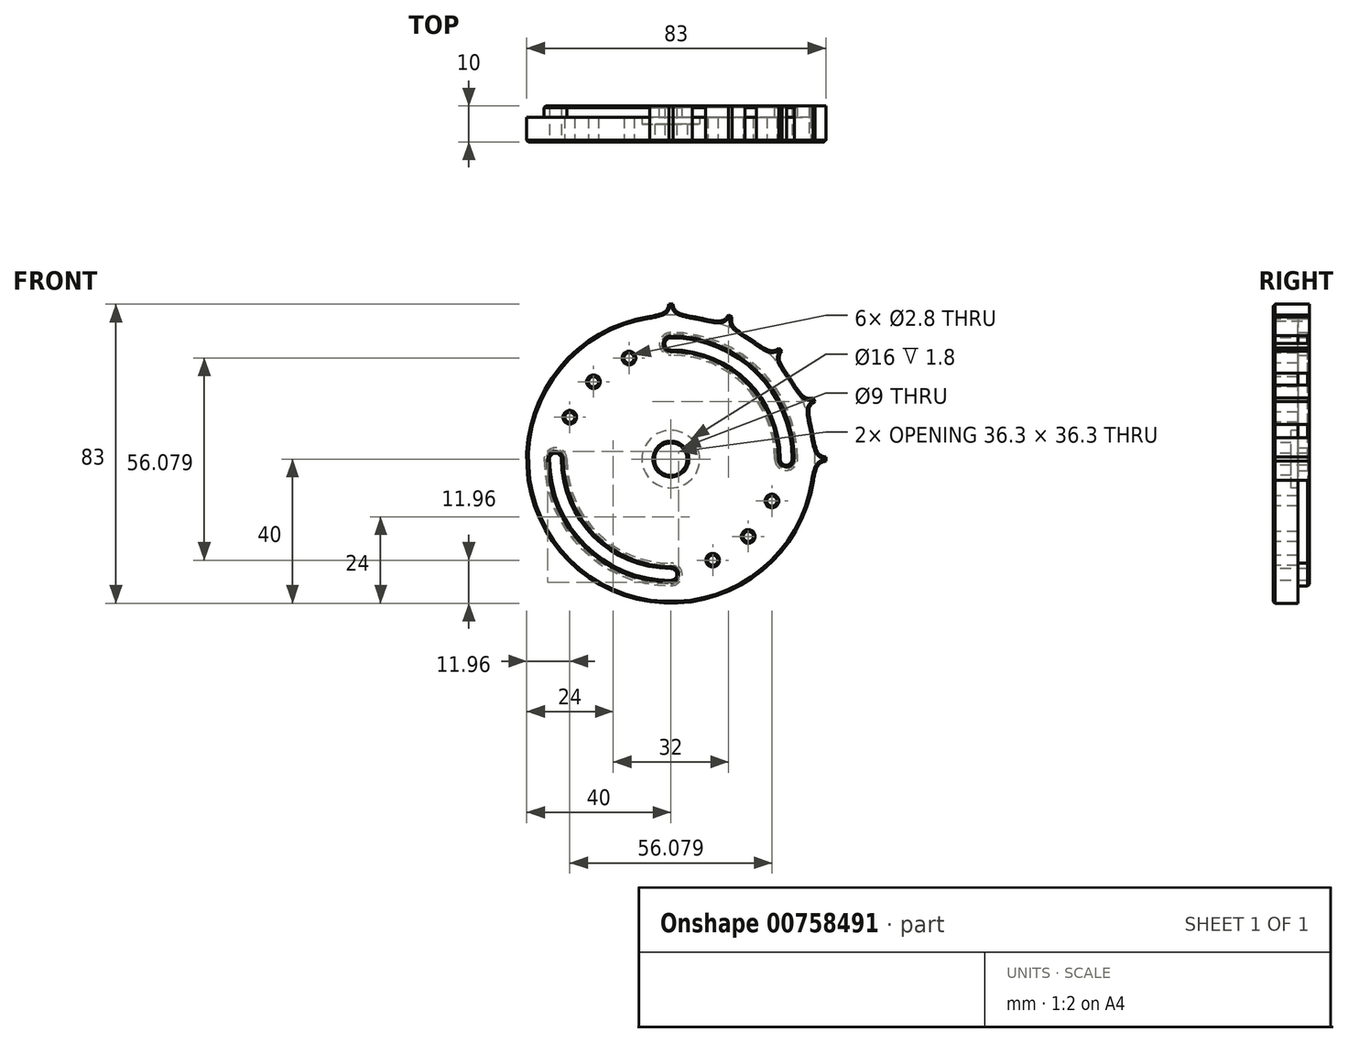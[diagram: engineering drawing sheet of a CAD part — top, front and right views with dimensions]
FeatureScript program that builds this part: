
annotation { "Feature Type Name" : "Feature", "Feature Type Description" : "" }
export const myFeature = defineFeature(function(context is Context, id is Id, definition is map)
    precondition{}
    {
        {
            var Q0;
            Q0=qCreatedBy(makeId("Front.planeOp"),FACE);
            var sketch = newSketch(context, id + "F0", { "sketchPlane" : qUnion([Q0])});
            skCircle(sketch, "E0", {"center": v(0, 0) * mm, "radius": 4.5 * mm});
            skCircle(sketch, "E1", {"center": v(0, 0) * mm, "radius": 40 * mm});
            skCircle(sketch, "E2", {"center": v(-32, 0) * mm, "radius": 1.65 * mm});
            skCircle(sketch, "E3.1.0", {"center": v(0, -32) * mm, "radius": 1.65 * mm});
            skCircle(sketch, "E3.2.0", {"center": v(32, 0) * mm, "radius": 1.65 * mm});
            skCircle(sketch, "E3.3.0", {"center": v(0, 32) * mm, "radius": 1.65 * mm});
            skCircle(sketch, "E4", {"center": v(0, 0) * mm, "radius": 8 * mm});
            skCircle(sketch, "E5", {"center": v(0, 0) * mm, "radius": 25 * mm});
            skCircle(sketch, "E6", {"center": v(0, 0) * mm, "radius": 33.65 * mm});
            skCircle(sketch, "E7", {"center": v(0, 0) * mm, "radius": 30.35 * mm});
            skCircle(sketch, "E8", {"center": v(-11.61, 28.04) * mm, "radius": 1.4 * mm});
            skCircle(sketch, "E9", {"center": v(-21.46, 21.46) * mm, "radius": 1.4 * mm});
            skLineSegment(sketch, "E10", {"start": v(0, 0) * mm, "end": v(-21.46, 21.46) * mm, "construction": true});
            skLineSegment(sketch, "E11", {"start": v(0, 0) * mm, "end": v(-11.61, 28.04) * mm, "construction": true});
            skCircle(sketch, "E12.MirrorC", {"center": v(-28.04, 11.61) * mm, "radius": 1.4 * mm});
            skCircle(sketch, "E13.1.0", {"center": v(11.61, -28.04) * mm, "radius": 1.4 * mm});
            skCircle(sketch, "E13.1.1", {"center": v(21.46, -21.46) * mm, "radius": 1.4 * mm});
            skCircle(sketch, "E13.1.2", {"center": v(28.04, -11.61) * mm, "radius": 1.4 * mm});
            skFitSpline(sketch, "E14", {"points": [v(43, 0.56) * mm, v(39.56, 5.91) * mm], "startDerivative": vector(-7.22, 1.17) * mm, "endDerivative": vector(-2.2, 10.93) * mm});
            skLineSegment(sketch, "E15", {"start": v(43, 0.56) * mm, "end": v(43, 0) * mm});
            skLineSegment(sketch, "E16.MirrorCS", {"start": v(43, -0.56) * mm, "end": v(43, 0) * mm});
            skFitSpline(sketch, "E17.MirrorCS", {"points": [v(43, -0.56) * mm, v(39.56, -5.91) * mm], "startDerivative": vector(-7.22, -1.17) * mm, "endDerivative": vector(-2.2, -10.93) * mm});
            skSolve(sketch);
        }
        {
            var Q0;
            Q0=makeQuery(id+"F0.imprint","IMPRINT",FACE,{"disambiguationData":[TD([[makeQuery(id+"F0.imprint","IMPRINT",EDGE,{"derivedFrom":sQuery(id+"F0.wireOp",EDGE,"E1")}),1.0]])]});
            var Q1;
            {var subQ0=sQuery(id+"F0.wireOp",EDGE,"E6");var subQ1=sQuery(id+"F0.wireOp",EDGE,"E2");var subQ2=makeQuery(id+"F0.imprint","INTERSECT",VERTEX,{"derivedFrom":[subQ1,subQ0]});Q1=makeQuery(id+"F0.imprint","IMPRINT",FACE,{"disambiguationData":[TD([[makeQuery(id+"F0.imprint","IMPRINT",EDGE,{"disambiguationData":[TD([[subQ2,1.0]])],"derivedFrom":subQ1}),-1.0]])]});}
            var Q2;
            Q2=makeQuery(id+"F0.imprint","IMPRINT",FACE,{"disambiguationData":[TD([[makeQuery(id+"F0.imprint","IMPRINT",EDGE,{"derivedFrom":sQuery(id+"F0.wireOp",EDGE,"E5")}),-1.0]])]});
            var Q3;
            {var subQ0=sQuery(id+"F0.wireOp",EDGE,"E6");var subQ1=sQuery(id+"F0.wireOp",EDGE,"E3.1.0");var subQ2=makeQuery(id+"F0.imprint","INTERSECT",VERTEX,{"derivedFrom":[subQ1,subQ0]});Q3=makeQuery(id+"F0.imprint","IMPRINT",FACE,{"disambiguationData":[TD([[makeQuery(id+"F0.imprint","IMPRINT",EDGE,{"disambiguationData":[TD([[subQ2,-1.0]])],"derivedFrom":subQ1}),-1.0]])]});}
            var Q4;
            Q4=makeQuery(id+"F0.imprint","IMPRINT",FACE,{"disambiguationData":[TD([[makeQuery(id+"F0.imprint","IMPRINT",EDGE,{"derivedFrom":sQuery(id+"F0.wireOp",EDGE,"E4")}),-1.0]])]});
            extrude(context, id + "F1", {"entities" : qUnion([Q0, Q1, Q2, Q3, Q4]), "oppositeDirection" : true, "depth" : 10 * mm, "offsetDistance" : 25 * mm});
        }
        {
            var Q0;
            Q0=makeQuery(id+"F0.imprint","IMPRINT",FACE,{"disambiguationData":[TD([[makeQuery(id+"F0.imprint","IMPRINT",EDGE,{"derivedFrom":sQuery(id+"F0.wireOp",EDGE,"E0")}),-1.0]])]});
            extrude(context, id + "F2", {"entities" : qUnion([Q0]), "operationType" : NewBodyOperationType.ADD, "oppositeDirection" : true, "depth" : 5 * mm, "offsetDistance" : 25 * mm});
        }
        {
            var Q0;
            Q0=makeQuery(id+"F1.opExtrude","CAP_FACE",FACE,{"disambiguationData":[OSD([sQuery(id+"F0.wireOp",EDGE,"E1"),sQuery(id+"F0.wireOp",EDGE,"E2"),sQuery(id+"F0.wireOp",EDGE,"E3.1.0"),sQuery(id+"F0.wireOp",EDGE,"E3.2.0"),sQuery(id+"F0.wireOp",EDGE,"E3.3.0"),sQuery(id+"F0.wireOp",EDGE,"E4"),sQuery(id+"F0.wireOp",EDGE,"E6"),sQuery(id+"F0.wireOp",EDGE,"E7")])],"isStart":false});
            var sketch = newSketch(context, id + "F3", { "sketchPlane" : qUnion([Q0])});
            skArc(sketch, "E18.0", {"start": v(-28.85, 0) * mm, "mid": v(-20.4, 20.4) * mm, "end": v(0, 28.85) * mm});
            skArc(sketch, "E18.1", {"start": v(-28.85, 0) * mm, "mid": v(-32, -3.15) * mm, "end": v(-35.15, 0) * mm});
            skArc(sketch, "E18.2", {"start": v(-35.15, 0) * mm, "mid": v(-24.85, 24.85) * mm, "end": v(0, 35.15) * mm});
            skArc(sketch, "E18.3", {"start": v(0, 35.15) * mm, "mid": v(3.15, 32) * mm, "end": v(0, 28.85) * mm});
            skArc(sketch, "E19.0", {"start": v(28.85, 0) * mm, "mid": v(20.4, -20.4) * mm, "end": v(0, -28.85) * mm});
            skArc(sketch, "E19.1", {"start": v(28.85, 0) * mm, "mid": v(32, 3.15) * mm, "end": v(35.15, 0) * mm});
            skArc(sketch, "E19.2", {"start": v(35.15, 0) * mm, "mid": v(24.85, -24.85) * mm, "end": v(0, -35.15) * mm});
            skArc(sketch, "E19.3", {"start": v(0, -35.15) * mm, "mid": v(-3.15, -32) * mm, "end": v(0, -28.85) * mm});
            skSolve(sketch);
        }
        {
            var Q0;
            Q0=makeQuery(id+"F3.imprint","IMPRINT",FACE,{"disambiguationData":[TD([[makeQuery(id+"F3.imprint","IMPRINT",EDGE,{"derivedFrom":sQuery(id+"F3.wireOp",EDGE,"E18.0")}),1.0]])]});
            var Q1;
            Q1=makeQuery(id+"F3.imprint","IMPRINT",FACE,{"disambiguationData":[TD([[makeQuery(id+"F3.imprint","IMPRINT",EDGE,{"derivedFrom":sQuery(id+"F3.wireOp",EDGE,"E19.0")}),1.0]])]});
            extrude(context, id + "F4", {"entities" : qUnion([Q0, Q1]), "operationType" : NewBodyOperationType.REMOVE, "oppositeDirection" : true, "depth" : 3.2 * mm, "offsetDistance" : 25 * mm});
        }
        {
            var Q0;
            {var subQ0=sQuery(id+"F0.wireOp",EDGE,"E14");Q0=makeQuery(id+"F0.imprint","IMPRINT",FACE,{"disambiguationData":[TD([[makeQuery(id+"F0.imprint","IMPRINT",EDGE,{"derivedFrom":subQ0}),1.0]])]});}
            var Q1;
            Q1=makeQuery(id+"F1.opExtrude","CAP_FACE",FACE,{"disambiguationData":[OSD([sQuery(id+"F0.wireOp",EDGE,"E1"),sQuery(id+"F0.wireOp",EDGE,"E2"),sQuery(id+"F0.wireOp",EDGE,"E3.1.0"),sQuery(id+"F0.wireOp",EDGE,"E3.2.0"),sQuery(id+"F0.wireOp",EDGE,"E3.3.0"),sQuery(id+"F0.wireOp",EDGE,"E4"),sQuery(id+"F0.wireOp",EDGE,"E6"),sQuery(id+"F0.wireOp",EDGE,"E7"),sQuery(id+"F0.wireOp",EDGE,"E8"),sQuery(id+"F0.wireOp",EDGE,"E9"),sQuery(id+"F0.wireOp",EDGE,"E12.MirrorC"),sQuery(id+"F0.wireOp",EDGE,"E13.1.0"),sQuery(id+"F0.wireOp",EDGE,"E13.1.1"),sQuery(id+"F0.wireOp",EDGE,"E13.1.2")])],"isStart":false});
            extrude(context, id + "F5", {"entities" : qUnion([Q0]), "endBound" : BoundingType.UP_TO_SURFACE, "oppositeDirection" : true, "depth" : 25 * mm, "endBoundEntityFace" : qUnion([Q1]), "offsetDistance" : 25 * mm});
        }
        {
            var Q0;
            Q0=makeQuery(id+"F5.opExtrude","SWEPT_BODY",BODY,{"disambiguationData":[OSD([sQuery(id+"F0.wireOp",EDGE,"E1"),sQuery(id+"F0.wireOp",EDGE,"E14"),sQuery(id+"F0.wireOp",EDGE,"E15"),sQuery(id+"F0.wireOp",EDGE,"E16.MirrorCS"),sQuery(id+"F0.wireOp",EDGE,"E17.MirrorCS")])]});
            var Q1;
            Q1=makeQuery(id+"F2.opExtrude","CAP_EDGE",EDGE,{"disambiguationData":[OSD([sQuery(id+"F0.wireOp",EDGE,"E0")])],"isStart":false});
            circularPattern(context, id + "F6", {"operationType" : NewBodyOperationType.ADD, "entities" : qUnion([Q0]), "axis" : qUnion([Q1]), "angle" : 90 * degree, "instanceCount" : 5, "equalSpace" : true});
        }
        {
            var Q0;
            Q0=makeQuery(id+"F1.opExtrude","CAP_FACE",FACE,{"disambiguationData":[OSD([sQuery(id+"F0.wireOp",EDGE,"E1"),sQuery(id+"F0.wireOp",EDGE,"E4")])],"isStart":true});
            var Q1;
            Q1=makeQuery(id+"F1.opExtrude","CAP_FACE",FACE,{"disambiguationData":[OSD([sQuery(id+"F0.wireOp",EDGE,"E1"),sQuery(id+"F0.wireOp",EDGE,"E2"),sQuery(id+"F0.wireOp",EDGE,"E3.1.0"),sQuery(id+"F0.wireOp",EDGE,"E3.2.0"),sQuery(id+"F0.wireOp",EDGE,"E3.3.0"),sQuery(id+"F0.wireOp",EDGE,"E4"),sQuery(id+"F0.wireOp",EDGE,"E6"),sQuery(id+"F0.wireOp",EDGE,"E7"),sQuery(id+"F0.wireOp",EDGE,"E8"),sQuery(id+"F0.wireOp",EDGE,"E9"),sQuery(id+"F0.wireOp",EDGE,"E12.MirrorC"),sQuery(id+"F0.wireOp",EDGE,"E13.1.0"),sQuery(id+"F0.wireOp",EDGE,"E13.1.1"),sQuery(id+"F0.wireOp",EDGE,"E13.1.2")])],"isStart":false});
            chamfer(context, id + "F7", {"entities" : qUnion([Q0, Q1]), "width" : 0.5 * mm, "tangentPropagation" : true});
        }
    });
